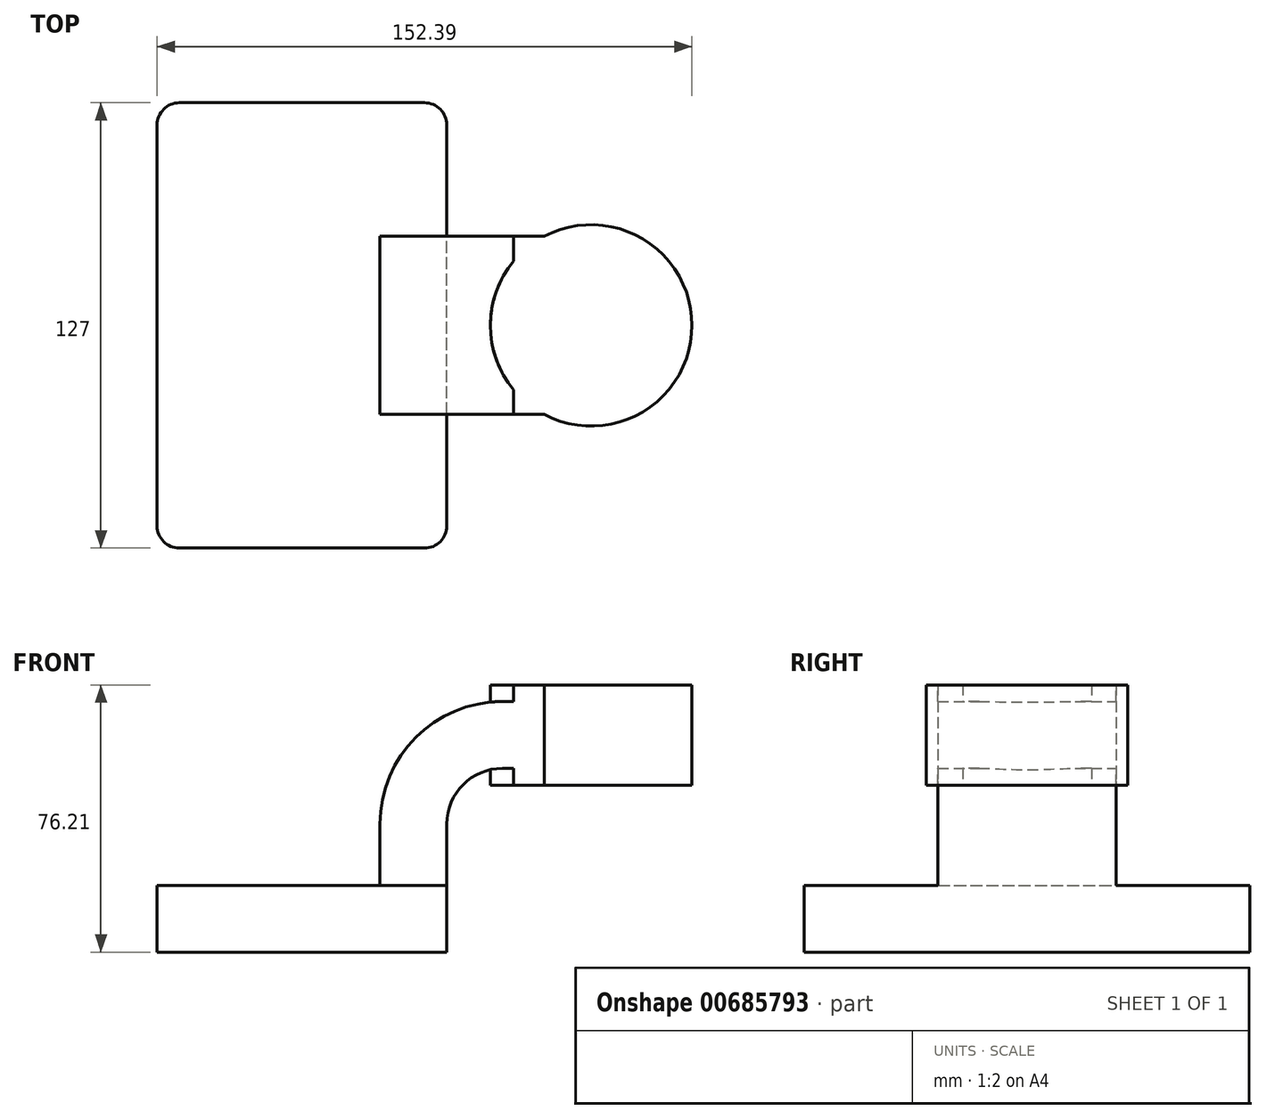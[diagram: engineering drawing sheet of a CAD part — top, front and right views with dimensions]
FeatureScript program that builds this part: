
annotation { "Feature Type Name" : "Feature", "Feature Type Description" : "" }
export const myFeature = defineFeature(function(context is Context, id is Id, definition is map)
    precondition{}
    {
        {
            var Q0;
            Q0=qCreatedBy(makeId("Front.planeOp"),FACE);
            var sketch = newSketch(context, id + "F0", { "sketchPlane" : qUnion([Q0])});
            skLineSegment(sketch, "E0.bottom", {"start": v(41.27, 9.53) * mm, "end": v(-41.28, 9.53) * mm});
            skLineSegment(sketch, "E0.top", {"start": v(41.28, -9.52) * mm, "end": v(-41.27, -9.52) * mm});
            skLineSegment(sketch, "E0.left", {"start": v(41.28, 9.53) * mm, "end": v(41.28, -9.52) * mm});
            skLineSegment(sketch, "E0.right", {"start": v(-41.28, 9.53) * mm, "end": v(-41.27, -9.52) * mm});
            skPoint(sketch, "E0.middle", {"position": v(0, 0) * mm});
            skLineSegment(sketch, "E1.bottom", {"start": v(111.12, 38.1) * mm, "end": v(60.32, 38.1) * mm});
            skLineSegment(sketch, "E1.top", {"start": v(111.12, 66.68) * mm, "end": v(60.32, 66.68) * mm});
            skLineSegment(sketch, "E1.left", {"start": v(111.12, 38.1) * mm, "end": v(111.12, 66.68) * mm});
            skLineSegment(sketch, "E1.right", {"start": v(60.32, 38.1) * mm, "end": v(60.32, 66.68) * mm});
            skPoint(sketch, "E1.middle", {"position": v(85.72, 52.39) * mm});
            skLineSegment(sketch, "E2", {"start": v(41.27, 9.53) * mm, "end": v(41.27, 27) * mm});
            skArc(sketch, "E3", {"start": v(41.27, 27) * mm, "mid": v(45.92, 38.23) * mm, "end": v(57.15, 42.88) * mm});
            skLineSegment(sketch, "E4", {"start": v(57.15, 42.88) * mm, "end": v(82.02, 42.88) * mm});
            skLineSegment(sketch, "E5.0", {"start": v(57.15, 61.93) * mm, "end": v(82.02, 61.93) * mm});
            skArc(sketch, "E5.1", {"start": v(22.23, 27) * mm, "mid": v(32.45, 51.7) * mm, "end": v(57.15, 61.93) * mm});
            skLineSegment(sketch, "E5.2", {"start": v(22.23, 9.53) * mm, "end": v(22.23, 27) * mm});
            skLineSegment(sketch, "E6", {"start": v(82.42, 38.1) * mm, "end": v(82.42, 66.68) * mm});
            skFitSpline(sketch, "E7", {"points": [v(-41.28, 9.53) * mm, v(57.15, 61.93) * mm], "startDerivative": vector(1.14, 90.6) * mm, "endDerivative": vector(142.05, -4.98) * mm});
            skSolve(sketch);
        }
        {
            var Q0;
            Q0=makeQuery(id+"F0.imprint","IMPRINT",FACE,{"disambiguationData":[TD([[makeQuery(id+"F0.imprint","IMPRINT",EDGE,{"derivedFrom":sQuery(id+"F0.wireOp",EDGE,"E0.top")}),-1.0]])]});
            extrude(context, id + "F1", {"entities" : qUnion([Q0]), "depth" : 127 * mm, "offsetDistance" : 25.4 * mm, "symmetric" : true});
        }
        {
            var Q0;
            {var subQ1=sQuery(id+"F0.wireOp",EDGE,"E2");Q0=makeQuery(id+"F0.imprint","IMPRINT",FACE,{"disambiguationData":[TD([[makeQuery(id+"F0.imprint","IMPRINT",EDGE,{"derivedFrom":subQ1}),1.0]])]});}
            var Q1;
            {var subQ6=sQuery(id+"F0.wireOp",EDGE,"E6");Q1=makeQuery(id+"F0.imprint","IMPRINT",FACE,{"disambiguationData":[TD([[makeQuery(id+"F0.imprint","IMPRINT",EDGE,{"derivedFrom":subQ6}),1.0]])]});}
            extrude(context, id + "F2", {"entities" : qUnion([Q0, Q1]), "operationType" : NewBodyOperationType.ADD, "depth" : 50.8 * mm, "offsetDistance" : 25.4 * mm, "symmetric" : true});
        }
        {
            var Q0;
            Q0=makeQuery(id+"F0.imprint","IMPRINT",FACE,{"disambiguationData":[TD([[makeQuery(id+"F0.imprint","IMPRINT",EDGE,{"derivedFrom":sQuery(id+"F0.wireOp",EDGE,"E5.1")}),1.0]])]});
            extrude(context, id + "F3", {"entities" : qUnion([Q0]), "operationType" : NewBodyOperationType.ADD, "depth" : 15.88 * mm, "offsetDistance" : 25.4 * mm, "symmetric" : true});
        }
        {
            var Q0;
            {var subQ0=sQuery(id+"F0.wireOp",EDGE,"E1.left");Q0=makeQuery(id+"F0.imprint","IMPRINT",FACE,{"disambiguationData":[TD([[makeQuery(id+"F0.imprint","IMPRINT",EDGE,{"derivedFrom":subQ0}),1.0]])]});}
            var Q1;
            Q1=sQuery(id+"F0.wireOp",EDGE,"E6");
            revolve(context, id + "F4", {"operationType" : NewBodyOperationType.ADD, "surfaceOperationType" : NewSurfaceOperationType.NEW, "entities" : qUnion([Q0]), "axis" : qUnion([Q1]), "revolveType" : RevolveType.FULL});
        }
        {
            var Q0;
            Q0=makeQuery(id+"F1.opExtrude","CAP_EDGE",EDGE,{"disambiguationData":[OSD([sQuery(id+"F0.wireOp",EDGE,"E0.right")])],"isStart":false});
            var Q1;
            Q1=makeQuery(id+"F1.opExtrude","CAP_EDGE",EDGE,{"disambiguationData":[OSD([sQuery(id+"F0.wireOp",EDGE,"E0.left")])],"isStart":false});
            var Q2;
            Q2=makeQuery(id+"F1.opExtrude","CAP_EDGE",EDGE,{"disambiguationData":[OSD([sQuery(id+"F0.wireOp",EDGE,"E0.left")])],"isStart":true});
            var Q3;
            Q3=makeQuery(id+"F1.opExtrude","CAP_EDGE",EDGE,{"disambiguationData":[OSD([sQuery(id+"F0.wireOp",EDGE,"E0.right")])],"isStart":true});
            fillet(context, id + "F5", {"entities" : qUnion([Q0, Q1, Q2, Q3]), "radius" : 6.35 * mm, "tangentPropagation" : true, "allowEdgeOverflow" : false});
        }
    });
